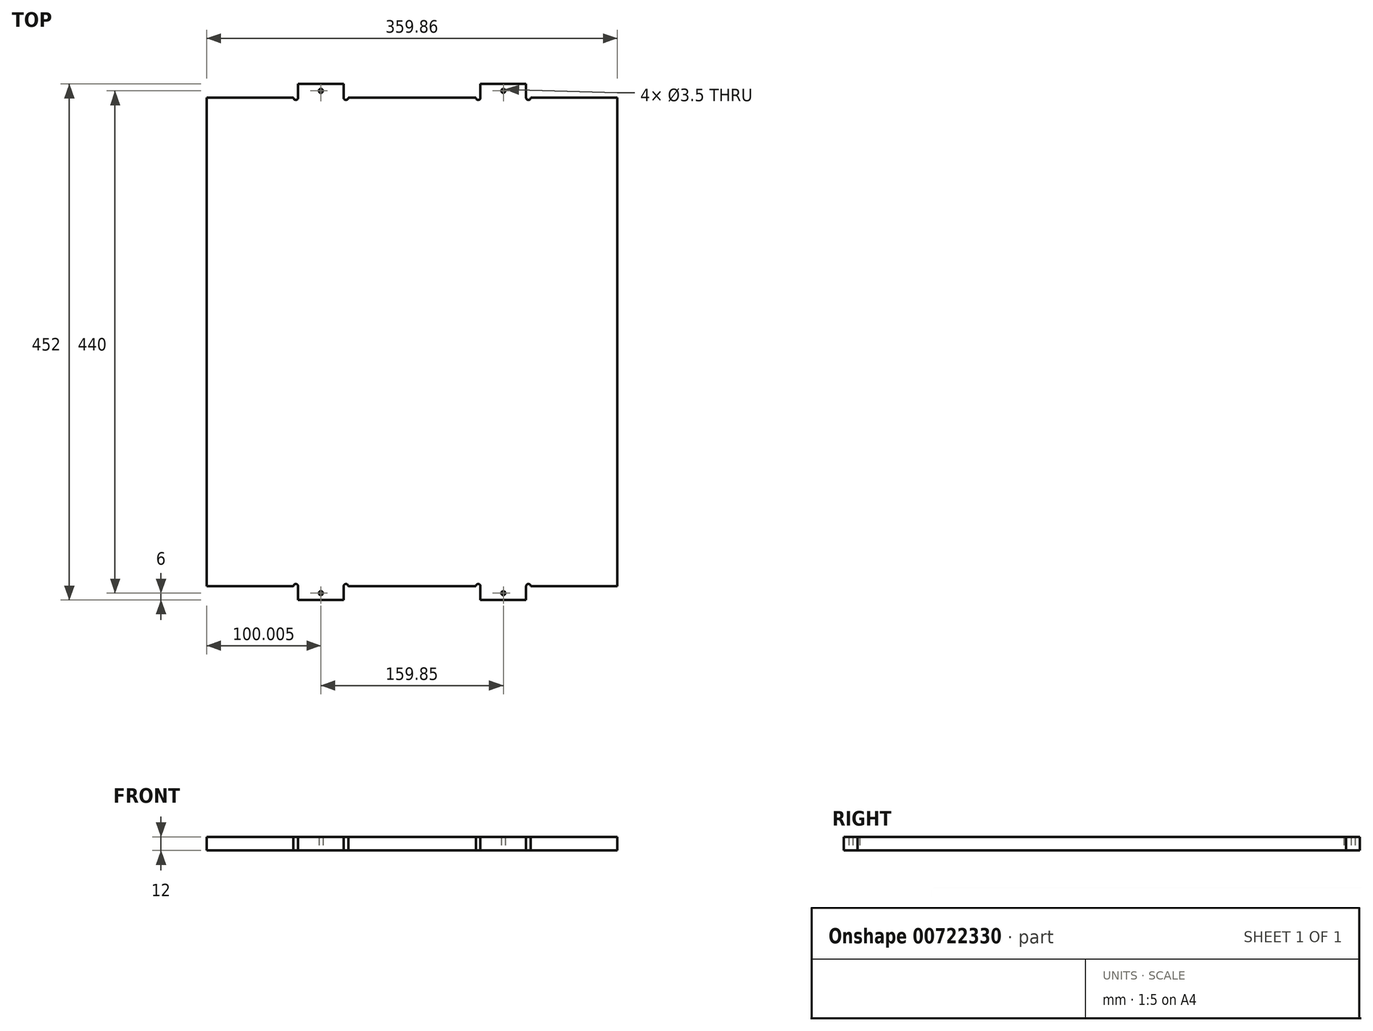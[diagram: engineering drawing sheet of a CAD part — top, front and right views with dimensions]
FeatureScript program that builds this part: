
annotation { "Feature Type Name" : "Feature", "Feature Type Description" : "" }
export const myFeature = defineFeature(function(context is Context, id is Id, definition is map)
    precondition{}
    {
        {
            var Q0;
            Q0=qCreatedBy(makeId("Top.planeOp"),FACE);
            var sketch = newSketch(context, id + "F0", { "sketchPlane" : qUnion([Q0])});
            skLineSegment(sketch, "E0", {"start": v(-179.93, 0) * mm, "end": v(-179.93, 214) * mm});
            skLineSegment(sketch, "E1", {"start": v(-179.93, 214) * mm, "end": v(-103.92, 214) * mm});
            skLineSegment(sketch, "E2", {"start": v(0, 214) * mm, "end": v(0, 0) * mm, "construction": true});
            skLineSegment(sketch, "E3", {"start": v(0, 0) * mm, "end": v(-179.93, 0) * mm, "construction": true});
            skLineSegment(sketch, "E4.top", {"start": v(-99.92, 226) * mm, "end": v(-59.93, 226) * mm});
            skLineSegment(sketch, "E4.left", {"start": v(-99.92, 214) * mm, "end": v(-99.92, 226) * mm});
            skLineSegment(sketch, "E4.right", {"start": v(-59.93, 214) * mm, "end": v(-59.93, 226) * mm});
            skLineSegment(sketch, "E5.trimOffspring", {"start": v(-55.93, 214) * mm, "end": v(0, 214) * mm});
            skArc(sketch, "E6", {"start": v(-99.92, 214) * mm, "mid": v(-101.92, 212) * mm, "end": v(-103.92, 214) * mm});
            skArc(sketch, "E7", {"start": v(-59.93, 214) * mm, "mid": v(-57.93, 212) * mm, "end": v(-55.93, 214) * mm});
            skLineSegment(sketch, "E8.MirrorCS", {"start": v(55.92, 214) * mm, "end": v(0, 214) * mm});
            skLineSegment(sketch, "E9.MirrorCS", {"start": v(59.93, 214) * mm, "end": v(59.93, 226) * mm});
            skLineSegment(sketch, "E10.MirrorCS", {"start": v(99.92, 226) * mm, "end": v(59.92, 226) * mm});
            skLineSegment(sketch, "E11.MirrorCS", {"start": v(99.92, 214) * mm, "end": v(99.92, 226) * mm});
            skLineSegment(sketch, "E12.MirrorCS", {"start": v(179.92, 214) * mm, "end": v(103.92, 214) * mm});
            skLineSegment(sketch, "E13.MirrorCS", {"start": v(179.93, 0) * mm, "end": v(179.93, 214) * mm});
            skArc(sketch, "E14.MirrorCS", {"start": v(59.92, 214) * mm, "mid": v(57.92, 212) * mm, "end": v(55.92, 214) * mm});
            skArc(sketch, "E15.MirrorCS", {"start": v(99.92, 214) * mm, "mid": v(101.92, 212) * mm, "end": v(103.92, 214) * mm});
            skLineSegment(sketch, "E16.MirrorCS", {"start": v(-179.93, 0) * mm, "end": v(-179.93, -214) * mm});
            skLineSegment(sketch, "E17.MirrorCS", {"start": v(-179.92, -214) * mm, "end": v(-103.92, -214) * mm});
            skArc(sketch, "E18.MirrorCS", {"start": v(-99.92, -214) * mm, "mid": v(-101.92, -212) * mm, "end": v(-103.92, -214) * mm});
            skLineSegment(sketch, "E19.MirrorCS", {"start": v(-99.92, -214) * mm, "end": v(-99.92, -226) * mm});
            skLineSegment(sketch, "E20.MirrorCS", {"start": v(-99.92, -226) * mm, "end": v(-59.92, -226) * mm});
            skLineSegment(sketch, "E21.MirrorCS", {"start": v(-59.93, -214) * mm, "end": v(-59.93, -226) * mm});
            skArc(sketch, "E22.MirrorCS", {"start": v(-59.92, -214) * mm, "mid": v(-57.92, -212) * mm, "end": v(-55.92, -214) * mm});
            skLineSegment(sketch, "E23.MirrorCS", {"start": v(-55.92, -214) * mm, "end": v(0, -214) * mm});
            skLineSegment(sketch, "E24.MirrorCS", {"start": v(55.93, -214) * mm, "end": v(0, -214) * mm});
            skArc(sketch, "E25.MirrorCS", {"start": v(59.93, -214) * mm, "mid": v(57.93, -212) * mm, "end": v(55.93, -214) * mm});
            skLineSegment(sketch, "E26.MirrorCS", {"start": v(59.93, -214) * mm, "end": v(59.93, -226) * mm});
            skLineSegment(sketch, "E27.MirrorCS", {"start": v(99.93, -226) * mm, "end": v(59.93, -226) * mm});
            skLineSegment(sketch, "E28.MirrorCS", {"start": v(99.92, -214) * mm, "end": v(99.92, -226) * mm});
            skArc(sketch, "E29.MirrorCS", {"start": v(99.93, -214) * mm, "mid": v(101.93, -212) * mm, "end": v(103.93, -214) * mm});
            skLineSegment(sketch, "E30.MirrorCS", {"start": v(179.93, -214) * mm, "end": v(103.93, -214) * mm});
            skLineSegment(sketch, "E31.MirrorCS", {"start": v(179.93, 0) * mm, "end": v(179.93, -214) * mm});
            skLineSegment(sketch, "E32", {"start": v(-99.92, 220) * mm, "end": v(-59.93, 220) * mm, "construction": true});
            skCircle(sketch, "E33", {"center": v(-79.93, 220) * mm, "radius": 1.75 * mm});
            skCircle(sketch, "E34.MirrorC", {"center": v(79.92, 220) * mm, "radius": 1.75 * mm});
            skCircle(sketch, "E35.MirrorC", {"center": v(-79.92, -220) * mm, "radius": 1.75 * mm});
            skCircle(sketch, "E36.MirrorC", {"center": v(79.93, -220) * mm, "radius": 1.75 * mm});
            skSolve(sketch);
        }
        {
            var Q0;
            Q0=makeQuery(id+"F0.imprint","IMPRINT",FACE,{"disambiguationData":[TD([[makeQuery(id+"F0.imprint","IMPRINT",EDGE,{"derivedFrom":sQuery(id+"F0.wireOp",EDGE,"E0")}),-1.0]])]});
            extrude(context, id + "F1", {"entities" : qUnion([Q0]), "depth" : 12 * mm, "offsetDistance" : 25 * mm});
        }
    });
